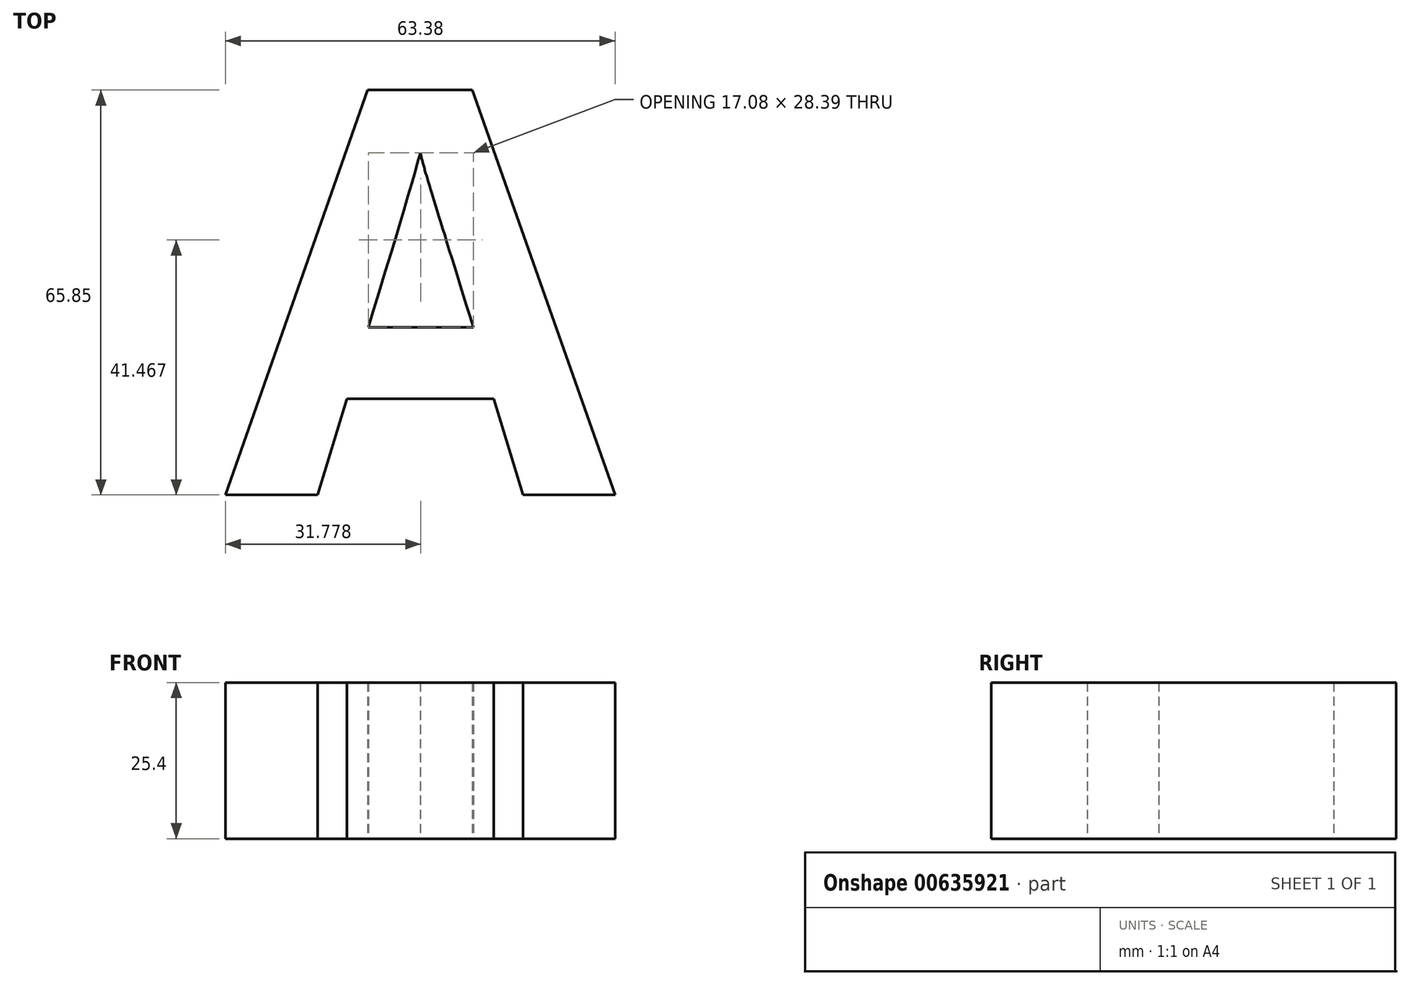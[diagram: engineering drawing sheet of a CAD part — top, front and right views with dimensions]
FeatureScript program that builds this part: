
annotation { "Feature Type Name" : "Feature", "Feature Type Description" : "" }
export const myFeature = defineFeature(function(context is Context, id is Id, definition is map)
    precondition{}
    {
        {
            var Q0;
            Q0=qCreatedBy(makeId("Top.planeOp"),FACE);
            var sketch = newSketch(context, id + "F0", { "sketchPlane" : qUnion([Q0])});
            skText(sketch, "E0", { "text": "A", "fontName": "OpenSans-Bold.ttf"});
            const initialGuessF0  = {"E0": [-0.03192, -0.02836, 1, 0, 0.06614]};
            skSetInitialGuess(sketch, initialGuessF0);
            skSolve(sketch);
        }
        {
            var Q0;
            Q0=makeQuery(id+"F0.imprint","IMPRINT",FACE,{"disambiguationData":[TD([[makeQuery(id+"F0.imprint","IMPRINT",EDGE,{"derivedFrom":sQuery(id+"F0.wireOp",EDGE,"E0.sketch_text.stroke-0")}),-1.0]])]});
            extrude(context, id + "F1", {"entities" : qUnion([Q0]), "depth" : 25.4 * mm, "offsetDistance" : 25.4 * mm});
        }
    });
